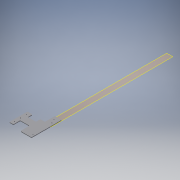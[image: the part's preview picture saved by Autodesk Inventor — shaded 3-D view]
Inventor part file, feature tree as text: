
AUTODESK INVENTOR PART (.ipt)
format: ipt  version: 2016 (Build 200138000, 138)  size: 168,448 bytes
history: native  units: mm
features: extrude x2, sketch x2, plane x1, fillet x1
ambient origin geometry x8: Origin, YZ Plane, XZ Plane, XY Plane, X Axis, Y Axis, Z Axis, Center Point
bodies: Solid1 (feature_tree)
feature tree (6):
  plane  "Work Plane1"
  extrude  "Extrusion1"  Depth=6.0mm TaperAngle=0.0deg
  fillet  "Fillet1"  Radius=92.0mm
  extrude  "Extrusion2"  Depth=40.0mm
  sketch  "Sketch1"  dims[d0=110.0mm d2=6.0mm d3=0.0mm d4=92.0mm]
  sketch  "Sketch2"  dims[d5=68.0mm d6=40.0mm d7=180.0mm d8=50.0mm d9=46.0mm d10=300.0mm d11=7.0mm d12=80.0mm d13=44.0mm d14=45.0mm d15=100.0mm d17=8.0mm d18=60.0mm d19=60.0mm d20=8.0mm d21=35.0mm d22=20.0mm d23=35.0mm d24=25.0mm d25=40.0mm d26=20.0mm d27=30.0mm d28=10.0mm d29=0.0mm]
